# Revit family: bimlib_narujnieblokisistemakondicionirovaniya_mrv-s-i_3hp_haier
name_source: partatom
category: Оборудование
units: mm (PartAtom-declared; Revit-internal decimal feet)

## family parameters
Всегда вертикально = Нет
На основе рабочей плоскости = Нет
Общий = Нет
При загрузке вырезать с полостями = Нет
Размер круглого соединителя = Использовать диаметр
Тип детали = Нормальный
Точка расчета площади = Нет

## types (1)
- AU032FSEUA_3HP_HAIER
    ADSK_URL документации изделия = https://haierproff.ru
    ADSK_URL страницы изделия = https://haierproff.ru
    ADSK_Версия Revit = 2017
    ADSK_Группирование = VRF-системы MRV S'
    ADSK_Единица измерения = шт.
    ADSK_Завод-изготовитель = Haier Group
    ADSK_Классификация нагрузок = ОВК
    ADSK_Код изделия = AU032FSEUA
    ADSK_Количество = 1
    ADSK_Количество фаз = 1
    ADSK_Коэффициент мощности = 1
    ADSK_Масса = 61
    ADSK_Наименование = Наружный блок VRF-системы кондиционирования MRV S', 3HP
    ADSK_Наименование краткое = VRF-системы MRV S', 3HP
    ADSK_Напряжение = 230 В
    ADSK_Номинальная мощность = 2200 Вт
    ADSK_Обозначение = MRV - S'
    ADSK_Полная мощность = 2200 В·А
    ADSK_Размер_Высота = 756 мм
    ADSK_Размер_Глубина = 372 мм
    ADSK_Размер_Ширина = 920 мм
    ADSK_Расход воздуха = 4500.0 м³/ч
    BL_BIM library = https://bimlib.pro
    HG_URL поставщика = www.haierproff.ru
    URL = www.haier.com
    Диаметр_Газ = 15.88 мм
    Диаметр_Жидкость = 9.52 мм
    Заправка хладагента = 2.10 кг
    Звуковое давление = 50
    Изготовитель = Haier Group
    Обогрев_Потребляемая мощность = 2 кВт
    Отметка по умолчанию = 0 мм
    Охлаждение_Потребляемая мощность = 2 кВт
    Производитель компрессора = MITSUBISHI ELECTRIC
    Работа на обогрев = Нет
    Рабочий диапазон_Обогрев = -20~ 27
    Рабочий диапазон_Охлаждение = -5 ~ 50
    Теплопроизводительность = 10 кВт
    Тип компрессора = Роторный
    Тип хладагента = R410A
    Холодопроизводительность = 8 кВт
    Частота тока = 50 Гц
